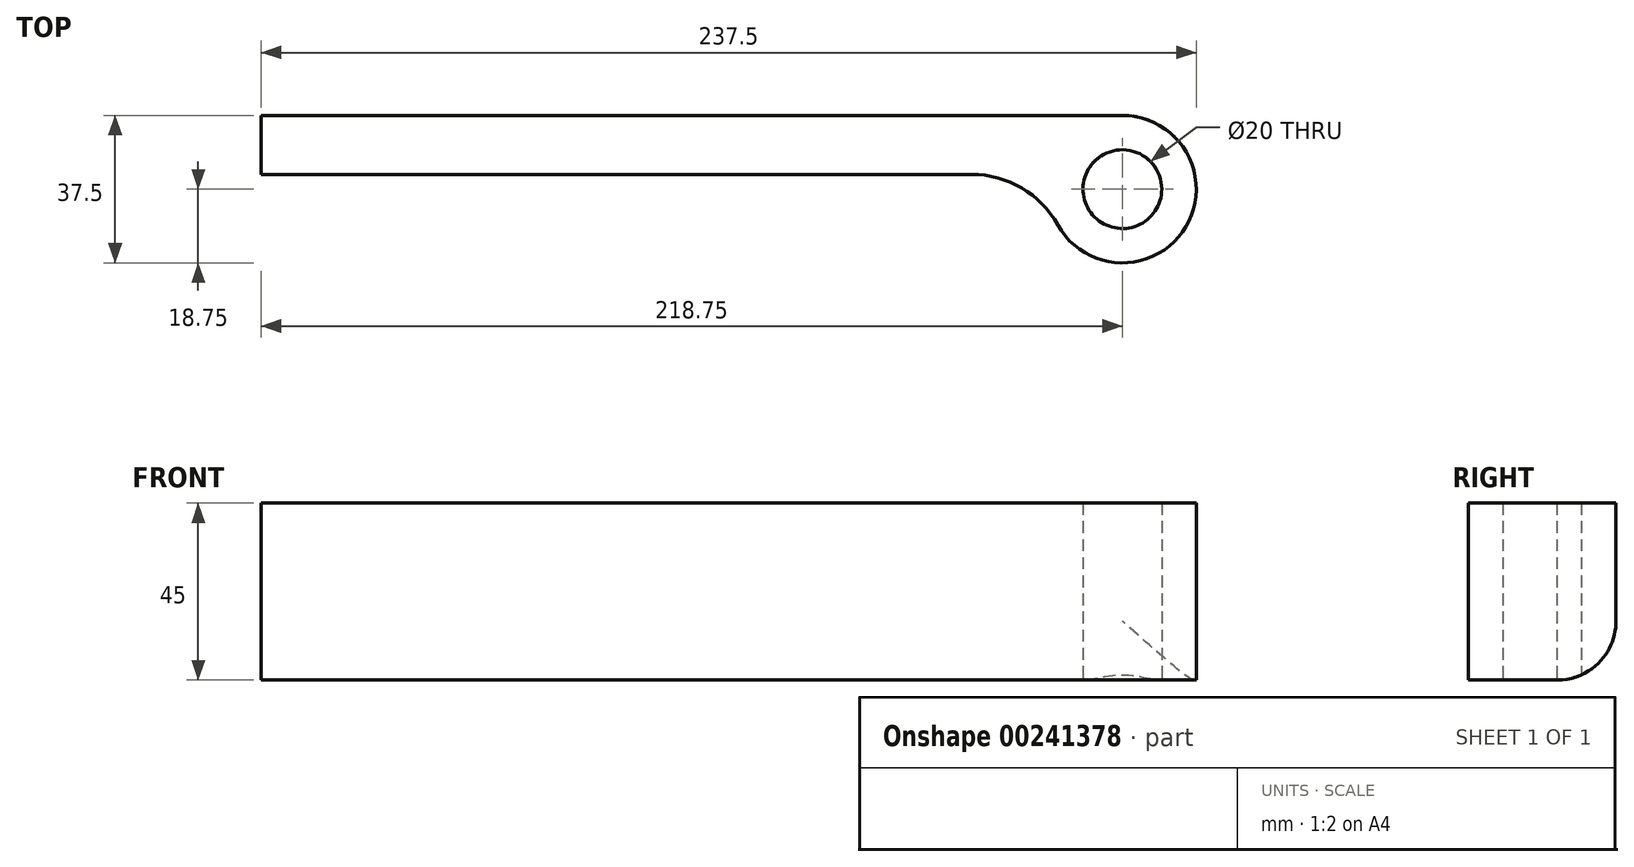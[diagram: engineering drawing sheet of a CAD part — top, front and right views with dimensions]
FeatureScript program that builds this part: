
annotation { "Feature Type Name" : "Feature", "Feature Type Description" : "" }
export const myFeature = defineFeature(function(context is Context, id is Id, definition is map)
    precondition{}
    {
        {
            var Q0;
            Q0=qCreatedBy(makeId("Top.planeOp"),FACE);
            var sketch = newSketch(context, id + "F0", { "sketchPlane" : qUnion([Q0])});
            skPoint(sketch, "E0.middle", {"position": v(0, 0) * mm});
            skLineSegment(sketch, "E1.bottom", {"start": v(118.75, 18.75) * mm, "end": v(81.25, 18.75) * mm});
            skLineSegment(sketch, "E1.top", {"start": v(118.75, -18.75) * mm, "end": v(81.25, -18.75) * mm});
            skLineSegment(sketch, "E1.right", {"start": v(81.25, 18.75) * mm, "end": v(81.25, -18.75) * mm});
            skCircle(sketch, "E2", {"center": v(100, 0) * mm, "radius": 10 * mm});
            skPoint(sketch, "E2.centerSnap0", {"position": v(100, 18.75) * mm});
            skLineSegment(sketch, "E3", {"start": v(81.25, 18.75) * mm, "end": v(-118.75, 18.75) * mm});
            skLineSegment(sketch, "E4", {"start": v(81.25, 3.75) * mm, "end": v(-118.75, 3.75) * mm});
            skLineSegment(sketch, "E5", {"start": v(-118.75, 18.75) * mm, "end": v(-118.75, 3.75) * mm});
            skLineSegment(sketch, "E6", {"start": v(118.75, 18.75) * mm, "end": v(118.75, -18.75) * mm});
            skSolve(sketch);
        }
        {
            var Q0;
            Q0 = qSketchRegion(id + "F0", true);
            extrude(context, id + "F1", {"entities" : qUnion([Q0]), "depth" : 45 * mm});
        }
        {
            var Q0;
            Q0=makeQuery(id+"F1.opExtrude","SWEPT_EDGE",EDGE,{"disambiguationData":[OSD([sQuery(id+"F0.wireOp",EDGE,"E1.bottom"),sQuery(id+"F0.wireOp",EDGE,"E1.left")])]});
            var Q1;
            Q1=makeQuery(id+"F1.opExtrude","SWEPT_EDGE",EDGE,{"disambiguationData":[OSD([sQuery(id+"F0.wireOp",EDGE,"E1.top"),sQuery(id+"F0.wireOp",EDGE,"E1.left")])]});
            fillet(context, id + "F2", {"entities" : qUnion([Q0, Q1]), "radius" : 18.75 * mm, "tangentPropagation" : true, "allowEdgeOverflow" : false});
        }
        {
            var Q0;
            Q0=makeQuery(id+"F1.opExtrude","SWEPT_EDGE",EDGE,{"disambiguationData":[OSD([sQuery(id+"F0.wireOp",EDGE,"E1.right"),sQuery(id+"F0.wireOp",EDGE,"E4")])]});
            fillet(context, id + "F3", {"entities" : qUnion([Q0]), "radius" : 25 * mm, "tangentPropagation" : true, "allowEdgeOverflow" : false});
        }
        {
            var Q0;
            Q0=makeQuery(id+"F1.opExtrude","CAP_EDGE",EDGE,{"disambiguationData":[OSD([sQuery(id+"F0.wireOp",EDGE,"E1.bottom"),sQuery(id+"F0.wireOp",EDGE,"E3")])],"isStart":true});
            fillet(context, id + "F4", {"entities" : qUnion([Q0]), "radius" : 15 * mm, "allowEdgeOverflow" : false});
        }
    });
